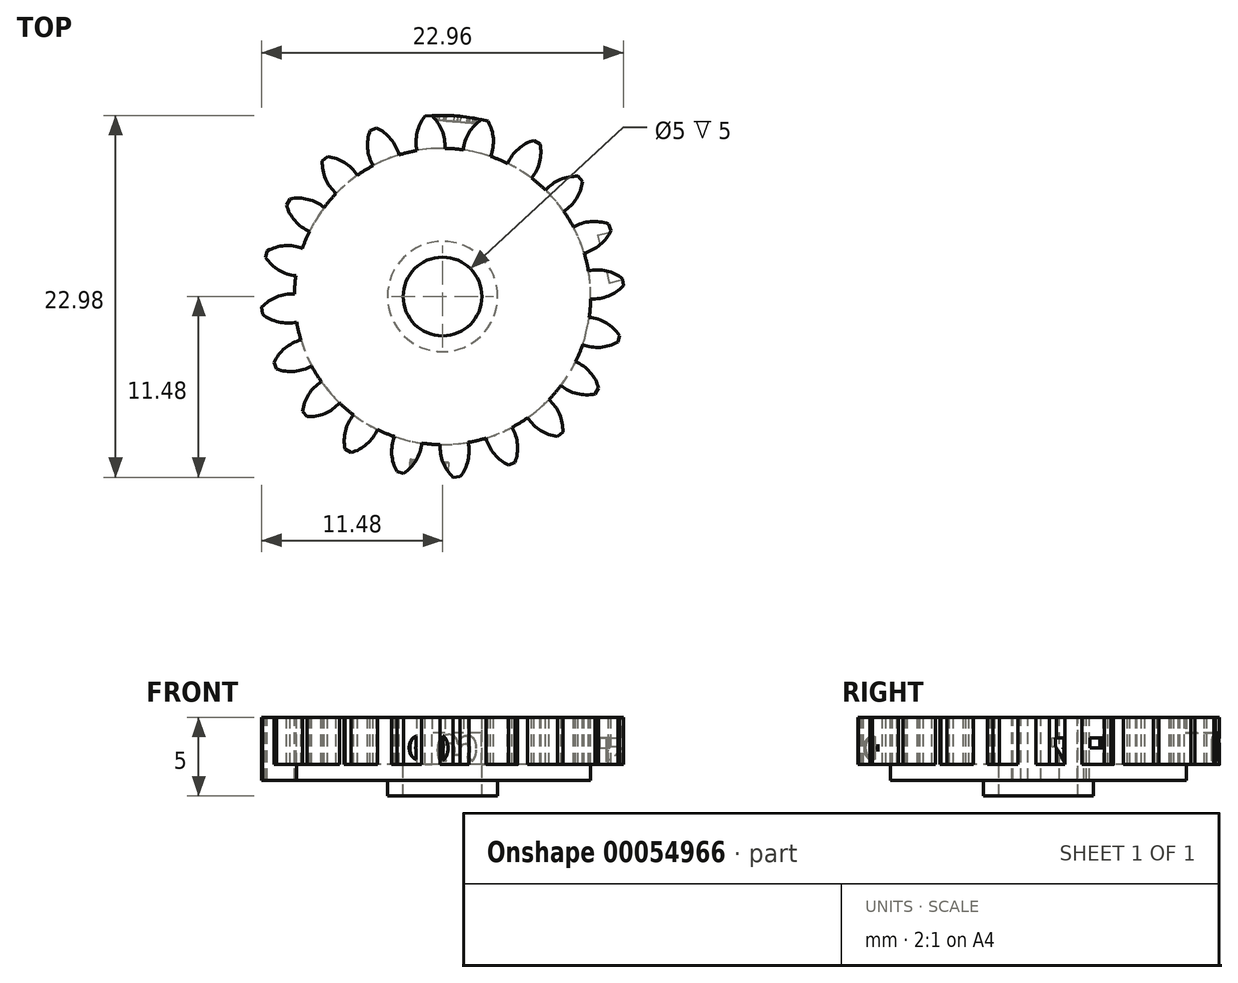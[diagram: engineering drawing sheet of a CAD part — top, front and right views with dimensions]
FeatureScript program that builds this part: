
annotation { "Feature Type Name" : "Feature", "Feature Type Description" : "" }
export const myFeature = defineFeature(function(context is Context, id is Id, definition is map)
    precondition{}
    {
        {
            assignVariable(context, id + "F0", {"name" : "GearDepth", "anyValue" : 1});
        }
        {
            var Q0;
            Q0=qCreatedBy(makeId("Top.planeOp"),FACE);
            var sketch = newSketch(context, id + "F1", { "sketchPlane" : qUnion([Q0])});
            skCircle(sketch, "E0", {"center": v(0, 0) * mm, "radius": 9.4 * mm});
            skCircle(sketch, "E1", {"center": v(0, 0) * mm, "radius": 10.45 * mm, "construction": true});
            skCircle(sketch, "E2", {"center": v(0, 0) * mm, "radius": 11.5 * mm});
            skLineSegment(sketch, "E3", {"start": v(0, 0) * mm, "end": v(0, 17.6) * mm, "construction": true});
            skLineSegment(sketch, "E4", {"start": v(0, 0) * mm, "end": v(-1.42, 18) * mm, "construction": true});
            skLineSegment(sketch, "E5", {"start": v(0, 10.45) * mm, "end": v(-10.54, 10.45) * mm, "construction": true});
            skLineSegment(sketch, "E6", {"start": v(0, 10.45) * mm, "end": v(-10.3, 6.7) * mm, "construction": true});
            skCircle(sketch, "E7", {"center": v(0, 10.45) * mm, "radius": 2.61 * mm, "construction": true});
            skCircle(sketch, "E8", {"center": v(-2.46, 9.56) * mm, "radius": 2.61 * mm, "construction": true});
            skArc(sketch, "E9", {"start": v(-4.91, 10.45) * mm, "mid": v(-4.92, 10.42) * mm, "end": v(-4.94, 10.39) * mm});
            skArc(sketch, "E10.trimOffspring", {"start": v(0.15, 9.4) * mm, "mid": v(-0.03, 10.54) * mm, "end": v(-0.68, 11.48) * mm});
            skArc(sketch, "E11.MirrorCS", {"start": v(-1.62, 9.27) * mm, "mid": v(-1.62, 10.41) * mm, "end": v(-1.12, 11.45) * mm});
            skLineSegment(sketch, "E12", {"start": v(-1.12, 11.45) * mm, "end": v(-0.68, 11.48) * mm});
            skArc(sketch, "E13.1.0", {"start": v(-2.76, 9) * mm, "mid": v(-3.29, 10.01) * mm, "end": v(-4.2, 10.7) * mm});
            skLineSegment(sketch, "E13.1.1", {"start": v(-4.6, 10.54) * mm, "end": v(-4.2, 10.7) * mm});
            skArc(sketch, "E13.1.2", {"start": v(-4.4, 8.31) * mm, "mid": v(-4.76, 9.4) * mm, "end": v(-4.6, 10.54) * mm});
            skArc(sketch, "E13.2.0", {"start": v(-5.4, 7.7) * mm, "mid": v(-6.22, 8.5) * mm, "end": v(-7.3, 8.89) * mm});
            skLineSegment(sketch, "E13.2.1", {"start": v(-7.64, 8.6) * mm, "end": v(-7.3, 8.89) * mm});
            skArc(sketch, "E13.2.2", {"start": v(-6.76, 6.54) * mm, "mid": v(-7.43, 7.47) * mm, "end": v(-7.64, 8.6) * mm});
            skArc(sketch, "E13.3.0", {"start": v(-7.52, 5.65) * mm, "mid": v(-8.54, 6.17) * mm, "end": v(-9.69, 6.2) * mm});
            skLineSegment(sketch, "E13.3.1", {"start": v(-9.92, 5.82) * mm, "end": v(-9.69, 6.2) * mm});
            skArc(sketch, "E13.3.2", {"start": v(-8.45, 4.13) * mm, "mid": v(-9.37, 4.81) * mm, "end": v(-9.92, 5.82) * mm});
            skArc(sketch, "E13.4.0", {"start": v(-8.9, 3.05) * mm, "mid": v(-10.03, 3.23) * mm, "end": v(-11.13, 2.9) * mm});
            skLineSegment(sketch, "E13.4.1", {"start": v(-11.23, 2.47) * mm, "end": v(-11.13, 2.9) * mm});
            skArc(sketch, "E13.4.2", {"start": v(-9.32, 1.32) * mm, "mid": v(-10.4, 1.68) * mm, "end": v(-11.23, 2.47) * mm});
            skArc(sketch, "E13.5.0", {"start": v(-9.4, 0.15) * mm, "mid": v(-10.54, -0.03) * mm, "end": v(-11.48, -0.68) * mm});
            skLineSegment(sketch, "E13.5.1", {"start": v(-11.45, -1.12) * mm, "end": v(-11.48, -0.68) * mm});
            skArc(sketch, "E13.5.2", {"start": v(-9.27, -1.62) * mm, "mid": v(-10.41, -1.62) * mm, "end": v(-11.45, -1.12) * mm});
            skArc(sketch, "E13.6.0", {"start": v(-9, -2.76) * mm, "mid": v(-10.01, -3.29) * mm, "end": v(-10.7, -4.2) * mm});
            skLineSegment(sketch, "E13.6.1", {"start": v(-10.54, -4.6) * mm, "end": v(-10.7, -4.2) * mm});
            skArc(sketch, "E13.6.2", {"start": v(-8.31, -4.4) * mm, "mid": v(-9.4, -4.76) * mm, "end": v(-10.54, -4.6) * mm});
            skArc(sketch, "E13.7.0", {"start": v(-7.7, -5.4) * mm, "mid": v(-8.5, -6.22) * mm, "end": v(-8.89, -7.3) * mm});
            skLineSegment(sketch, "E13.7.1", {"start": v(-8.6, -7.64) * mm, "end": v(-8.89, -7.3) * mm});
            skArc(sketch, "E13.7.2", {"start": v(-6.54, -6.76) * mm, "mid": v(-7.47, -7.43) * mm, "end": v(-8.6, -7.64) * mm});
            skArc(sketch, "E13.8.0", {"start": v(-5.65, -7.52) * mm, "mid": v(-6.17, -8.54) * mm, "end": v(-6.2, -9.69) * mm});
            skLineSegment(sketch, "E13.8.1", {"start": v(-5.82, -9.92) * mm, "end": v(-6.2, -9.69) * mm});
            skArc(sketch, "E13.8.2", {"start": v(-4.13, -8.45) * mm, "mid": v(-4.81, -9.37) * mm, "end": v(-5.82, -9.92) * mm});
            skArc(sketch, "E13.9.0", {"start": v(-3.05, -8.9) * mm, "mid": v(-3.23, -10.03) * mm, "end": v(-2.9, -11.13) * mm});
            skLineSegment(sketch, "E13.9.1", {"start": v(-2.47, -11.23) * mm, "end": v(-2.9, -11.13) * mm});
            skArc(sketch, "E13.9.2", {"start": v(-1.32, -9.32) * mm, "mid": v(-1.68, -10.4) * mm, "end": v(-2.47, -11.23) * mm});
            skArc(sketch, "E13.10.0", {"start": v(-0.15, -9.4) * mm, "mid": v(0.03, -10.54) * mm, "end": v(0.68, -11.48) * mm});
            skLineSegment(sketch, "E13.10.1", {"start": v(1.12, -11.45) * mm, "end": v(0.68, -11.48) * mm});
            skArc(sketch, "E13.10.2", {"start": v(1.62, -9.27) * mm, "mid": v(1.62, -10.41) * mm, "end": v(1.12, -11.45) * mm});
            skArc(sketch, "E13.11.0", {"start": v(2.76, -9) * mm, "mid": v(3.29, -10.01) * mm, "end": v(4.2, -10.7) * mm});
            skLineSegment(sketch, "E13.11.1", {"start": v(4.6, -10.54) * mm, "end": v(4.2, -10.7) * mm});
            skArc(sketch, "E13.11.2", {"start": v(4.4, -8.31) * mm, "mid": v(4.76, -9.4) * mm, "end": v(4.6, -10.54) * mm});
            skArc(sketch, "E13.12.0", {"start": v(5.4, -7.7) * mm, "mid": v(6.22, -8.5) * mm, "end": v(7.3, -8.89) * mm});
            skLineSegment(sketch, "E13.12.1", {"start": v(7.64, -8.6) * mm, "end": v(7.3, -8.89) * mm});
            skArc(sketch, "E13.12.2", {"start": v(6.76, -6.54) * mm, "mid": v(7.43, -7.47) * mm, "end": v(7.64, -8.6) * mm});
            skArc(sketch, "E13.13.0", {"start": v(7.52, -5.65) * mm, "mid": v(8.54, -6.17) * mm, "end": v(9.69, -6.2) * mm});
            skLineSegment(sketch, "E13.13.1", {"start": v(9.92, -5.82) * mm, "end": v(9.69, -6.2) * mm});
            skArc(sketch, "E13.13.2", {"start": v(8.45, -4.13) * mm, "mid": v(9.37, -4.81) * mm, "end": v(9.92, -5.82) * mm});
            skArc(sketch, "E13.14.0", {"start": v(8.9, -3.05) * mm, "mid": v(10.03, -3.23) * mm, "end": v(11.13, -2.9) * mm});
            skLineSegment(sketch, "E13.14.1", {"start": v(11.23, -2.47) * mm, "end": v(11.13, -2.9) * mm});
            skArc(sketch, "E13.14.2", {"start": v(9.32, -1.32) * mm, "mid": v(10.4, -1.68) * mm, "end": v(11.23, -2.47) * mm});
            skArc(sketch, "E13.15.0", {"start": v(9.4, -0.15) * mm, "mid": v(10.54, 0.03) * mm, "end": v(11.48, 0.68) * mm});
            skLineSegment(sketch, "E13.15.1", {"start": v(11.45, 1.12) * mm, "end": v(11.48, 0.68) * mm});
            skArc(sketch, "E13.15.2", {"start": v(9.27, 1.62) * mm, "mid": v(10.41, 1.62) * mm, "end": v(11.45, 1.12) * mm});
            skArc(sketch, "E13.16.0", {"start": v(9, 2.76) * mm, "mid": v(10.01, 3.29) * mm, "end": v(10.7, 4.2) * mm});
            skLineSegment(sketch, "E13.16.1", {"start": v(10.54, 4.6) * mm, "end": v(10.7, 4.2) * mm});
            skArc(sketch, "E13.16.2", {"start": v(8.31, 4.4) * mm, "mid": v(9.4, 4.76) * mm, "end": v(10.54, 4.6) * mm});
            skArc(sketch, "E13.17.0", {"start": v(7.7, 5.4) * mm, "mid": v(8.5, 6.22) * mm, "end": v(8.89, 7.3) * mm});
            skLineSegment(sketch, "E13.17.1", {"start": v(8.6, 7.64) * mm, "end": v(8.89, 7.3) * mm});
            skArc(sketch, "E13.17.2", {"start": v(6.54, 6.76) * mm, "mid": v(7.47, 7.43) * mm, "end": v(8.6, 7.64) * mm});
            skArc(sketch, "E13.18.0", {"start": v(5.65, 7.52) * mm, "mid": v(6.17, 8.54) * mm, "end": v(6.2, 9.69) * mm});
            skLineSegment(sketch, "E13.18.1", {"start": v(5.82, 9.92) * mm, "end": v(6.2, 9.69) * mm});
            skArc(sketch, "E13.18.2", {"start": v(4.13, 8.45) * mm, "mid": v(4.81, 9.37) * mm, "end": v(5.82, 9.92) * mm});
            skArc(sketch, "E13.19.0", {"start": v(3.05, 8.9) * mm, "mid": v(3.23, 10.03) * mm, "end": v(2.9, 11.13) * mm});
            skLineSegment(sketch, "E13.19.1", {"start": v(2.47, 11.23) * mm, "end": v(2.9, 11.13) * mm});
            skArc(sketch, "E13.19.2", {"start": v(1.32, 9.32) * mm, "mid": v(1.68, 10.4) * mm, "end": v(2.47, 11.23) * mm});
            skCircle(sketch, "E14", {"center": v(0, 0) * mm, "radius": 2.5 * mm});
            skCircle(sketch, "E15", {"center": v(0, 0) * mm, "radius": 3.5 * mm});
            skPoint(sketch, "E16", {"position": v(-11.47, 0.86) * mm});
            skSolve(sketch);
        }
        {
            var Q0;
            {var subQ0=sQuery(id+"F1.wireOp",EDGE,"E13.5.0");Q0=makeQuery(id+"F1.imprint","IMPRINT",FACE,{"disambiguationData":[TD([[makeQuery(id+"F1.imprint","IMPRINT",EDGE,{"derivedFrom":subQ0}),1.0]])]});}
            var Q1;
            {var subQ0=sQuery(id+"F1.wireOp",EDGE,"E13.4.0");Q1=makeQuery(id+"F1.imprint","IMPRINT",FACE,{"disambiguationData":[TD([[makeQuery(id+"F1.imprint","IMPRINT",EDGE,{"derivedFrom":subQ0}),1.0]])]});}
            var Q2;
            Q2=makeQuery(id+"F1.imprint","IMPRINT",FACE,{"disambiguationData":[TD([[makeQuery(id+"F1.imprint","IMPRINT",EDGE,{"derivedFrom":sQuery(id+"F1.wireOp",EDGE,"E14")}),-1.0]])]});
            var Q3;
            Q3=makeQuery(id+"F1.imprint","IMPRINT",FACE,{"disambiguationData":[TD([[makeQuery(id+"F1.imprint","IMPRINT",EDGE,{"derivedFrom":sQuery(id+"F1.wireOp",EDGE,"E15")}),-1.0]])]});
            extrude(context, id + "F2", {"entities" : qUnion([Q0, Q1, Q2, Q3]), "oppositeDirection" : true, "depth" : 3 * mm});
        }
        {
            var Q0;
            Q0=makeQuery(id+"F1.imprint","IMPRINT",FACE,{"disambiguationData":[TD([[makeQuery(id+"F1.imprint","IMPRINT",EDGE,{"derivedFrom":sQuery(id+"F1.wireOp",EDGE,"E14")}),-1.0]])]});
            var Q1;
            {var subQ0=sQuery(id+"F1.wireOp",EDGE,"E13.10.2");Q1=makeQuery(id+"F1.imprint","IMPRINT",FACE,{"disambiguationData":[TD([[makeQuery(id+"F1.imprint","IMPRINT",EDGE,{"derivedFrom":subQ0}),1.0]])]});}
            var Q2;
            {var subQ0=sQuery(id+"F1.wireOp",EDGE,"E13.11.0");Q2=makeQuery(id+"F1.imprint","IMPRINT",FACE,{"disambiguationData":[TD([[makeQuery(id+"F1.imprint","IMPRINT",EDGE,{"derivedFrom":subQ0}),1.0]])]});}
            var Q3;
            {var subQ0=sQuery(id+"F1.wireOp",EDGE,"E13.11.2");Q3=makeQuery(id+"F1.imprint","IMPRINT",FACE,{"disambiguationData":[TD([[makeQuery(id+"F1.imprint","IMPRINT",EDGE,{"derivedFrom":subQ0}),1.0]])]});}
            var Q4;
            {var subQ0=sQuery(id+"F1.wireOp",EDGE,"E13.12.0");Q4=makeQuery(id+"F1.imprint","IMPRINT",FACE,{"disambiguationData":[TD([[makeQuery(id+"F1.imprint","IMPRINT",EDGE,{"derivedFrom":subQ0}),1.0]])]});}
            var Q5;
            {var subQ0=sQuery(id+"F1.wireOp",EDGE,"E13.12.2");Q5=makeQuery(id+"F1.imprint","IMPRINT",FACE,{"disambiguationData":[TD([[makeQuery(id+"F1.imprint","IMPRINT",EDGE,{"derivedFrom":subQ0}),1.0]])]});}
            var Q6;
            {var subQ0=sQuery(id+"F1.wireOp",EDGE,"E13.13.0");Q6=makeQuery(id+"F1.imprint","IMPRINT",FACE,{"disambiguationData":[TD([[makeQuery(id+"F1.imprint","IMPRINT",EDGE,{"derivedFrom":subQ0}),1.0]])]});}
            var Q7;
            {var subQ0=sQuery(id+"F1.wireOp",EDGE,"E13.13.2");Q7=makeQuery(id+"F1.imprint","IMPRINT",FACE,{"disambiguationData":[TD([[makeQuery(id+"F1.imprint","IMPRINT",EDGE,{"derivedFrom":subQ0}),1.0]])]});}
            var Q8;
            {var subQ0=sQuery(id+"F1.wireOp",EDGE,"E13.14.0");Q8=makeQuery(id+"F1.imprint","IMPRINT",FACE,{"disambiguationData":[TD([[makeQuery(id+"F1.imprint","IMPRINT",EDGE,{"derivedFrom":subQ0}),1.0]])]});}
            var Q9;
            {var subQ0=sQuery(id+"F1.wireOp",EDGE,"E13.14.2");Q9=makeQuery(id+"F1.imprint","IMPRINT",FACE,{"disambiguationData":[TD([[makeQuery(id+"F1.imprint","IMPRINT",EDGE,{"derivedFrom":subQ0}),1.0]])]});}
            var Q10;
            {var subQ0=sQuery(id+"F1.wireOp",EDGE,"E13.15.0");Q10=makeQuery(id+"F1.imprint","IMPRINT",FACE,{"disambiguationData":[TD([[makeQuery(id+"F1.imprint","IMPRINT",EDGE,{"derivedFrom":subQ0}),1.0]])]});}
            var Q11;
            {var subQ0=sQuery(id+"F1.wireOp",EDGE,"E13.15.2");Q11=makeQuery(id+"F1.imprint","IMPRINT",FACE,{"disambiguationData":[TD([[makeQuery(id+"F1.imprint","IMPRINT",EDGE,{"derivedFrom":subQ0}),1.0]])]});}
            var Q12;
            {var subQ0=sQuery(id+"F1.wireOp",EDGE,"E13.16.0");Q12=makeQuery(id+"F1.imprint","IMPRINT",FACE,{"disambiguationData":[TD([[makeQuery(id+"F1.imprint","IMPRINT",EDGE,{"derivedFrom":subQ0}),1.0]])]});}
            var Q13;
            {var subQ0=sQuery(id+"F1.wireOp",EDGE,"E13.16.2");Q13=makeQuery(id+"F1.imprint","IMPRINT",FACE,{"disambiguationData":[TD([[makeQuery(id+"F1.imprint","IMPRINT",EDGE,{"derivedFrom":subQ0}),1.0]])]});}
            var Q14;
            {var subQ0=sQuery(id+"F1.wireOp",EDGE,"E13.17.0");Q14=makeQuery(id+"F1.imprint","IMPRINT",FACE,{"disambiguationData":[TD([[makeQuery(id+"F1.imprint","IMPRINT",EDGE,{"derivedFrom":subQ0}),1.0]])]});}
            var Q15;
            {var subQ0=sQuery(id+"F1.wireOp",EDGE,"E13.17.2");Q15=makeQuery(id+"F1.imprint","IMPRINT",FACE,{"disambiguationData":[TD([[makeQuery(id+"F1.imprint","IMPRINT",EDGE,{"derivedFrom":subQ0}),1.0]])]});}
            var Q16;
            {var subQ0=sQuery(id+"F1.wireOp",EDGE,"E13.18.0");Q16=makeQuery(id+"F1.imprint","IMPRINT",FACE,{"disambiguationData":[TD([[makeQuery(id+"F1.imprint","IMPRINT",EDGE,{"derivedFrom":subQ0}),1.0]])]});}
            var Q17;
            {var subQ0=sQuery(id+"F1.wireOp",EDGE,"E13.18.2");Q17=makeQuery(id+"F1.imprint","IMPRINT",FACE,{"disambiguationData":[TD([[makeQuery(id+"F1.imprint","IMPRINT",EDGE,{"derivedFrom":subQ0}),1.0]])]});}
            var Q18;
            {var subQ0=sQuery(id+"F1.wireOp",EDGE,"E13.19.0");Q18=makeQuery(id+"F1.imprint","IMPRINT",FACE,{"disambiguationData":[TD([[makeQuery(id+"F1.imprint","IMPRINT",EDGE,{"derivedFrom":subQ0}),1.0]])]});}
            var Q19;
            {var subQ0=sQuery(id+"F1.wireOp",EDGE,"E10.trimOffspring");Q19=makeQuery(id+"F1.imprint","IMPRINT",FACE,{"disambiguationData":[TD([[makeQuery(id+"F1.imprint","IMPRINT",EDGE,{"derivedFrom":subQ0}),-1.0]])]});}
            var Q20;
            {var subQ0=sQuery(id+"F1.wireOp",EDGE,"E10.trimOffspring");Q20=makeQuery(id+"F1.imprint","IMPRINT",FACE,{"disambiguationData":[TD([[makeQuery(id+"F1.imprint","IMPRINT",EDGE,{"derivedFrom":subQ0}),1.0]])]});}
            var Q21;
            {var subQ0=sQuery(id+"F1.wireOp",EDGE,"E11.MirrorCS");Q21=makeQuery(id+"F1.imprint","IMPRINT",FACE,{"disambiguationData":[TD([[makeQuery(id+"F1.imprint","IMPRINT",EDGE,{"derivedFrom":subQ0}),1.0]])]});}
            var Q22;
            {var subQ0=sQuery(id+"F1.wireOp",EDGE,"E13.1.0");Q22=makeQuery(id+"F1.imprint","IMPRINT",FACE,{"disambiguationData":[TD([[makeQuery(id+"F1.imprint","IMPRINT",EDGE,{"derivedFrom":subQ0}),1.0]])]});}
            var Q23;
            {var subQ0=sQuery(id+"F1.wireOp",EDGE,"E13.1.2");Q23=makeQuery(id+"F1.imprint","IMPRINT",FACE,{"disambiguationData":[TD([[makeQuery(id+"F1.imprint","IMPRINT",EDGE,{"derivedFrom":subQ0}),1.0]])]});}
            var Q24;
            {var subQ0=sQuery(id+"F1.wireOp",EDGE,"E13.2.0");Q24=makeQuery(id+"F1.imprint","IMPRINT",FACE,{"disambiguationData":[TD([[makeQuery(id+"F1.imprint","IMPRINT",EDGE,{"derivedFrom":subQ0}),1.0]])]});}
            var Q25;
            {var subQ0=sQuery(id+"F1.wireOp",EDGE,"E13.2.2");Q25=makeQuery(id+"F1.imprint","IMPRINT",FACE,{"disambiguationData":[TD([[makeQuery(id+"F1.imprint","IMPRINT",EDGE,{"derivedFrom":subQ0}),1.0]])]});}
            var Q26;
            {var subQ0=sQuery(id+"F1.wireOp",EDGE,"E13.3.0");Q26=makeQuery(id+"F1.imprint","IMPRINT",FACE,{"disambiguationData":[TD([[makeQuery(id+"F1.imprint","IMPRINT",EDGE,{"derivedFrom":subQ0}),1.0]])]});}
            var Q27;
            {var subQ0=sQuery(id+"F1.wireOp",EDGE,"E13.3.2");Q27=makeQuery(id+"F1.imprint","IMPRINT",FACE,{"disambiguationData":[TD([[makeQuery(id+"F1.imprint","IMPRINT",EDGE,{"derivedFrom":subQ0}),1.0]])]});}
            var Q28;
            {var subQ0=sQuery(id+"F1.wireOp",EDGE,"E13.4.0");Q28=makeQuery(id+"F1.imprint","IMPRINT",FACE,{"disambiguationData":[TD([[makeQuery(id+"F1.imprint","IMPRINT",EDGE,{"derivedFrom":subQ0}),1.0]])]});}
            var Q29;
            {var subQ0=sQuery(id+"F1.wireOp",EDGE,"E13.4.2");Q29=makeQuery(id+"F1.imprint","IMPRINT",FACE,{"disambiguationData":[TD([[makeQuery(id+"F1.imprint","IMPRINT",EDGE,{"derivedFrom":subQ0}),1.0]])]});}
            var Q30;
            {var subQ0=sQuery(id+"F1.wireOp",EDGE,"E13.5.0");Q30=makeQuery(id+"F1.imprint","IMPRINT",FACE,{"disambiguationData":[TD([[makeQuery(id+"F1.imprint","IMPRINT",EDGE,{"derivedFrom":subQ0}),1.0]])]});}
            var Q31;
            {var subQ0=sQuery(id+"F1.wireOp",EDGE,"E13.5.2");Q31=makeQuery(id+"F1.imprint","IMPRINT",FACE,{"disambiguationData":[TD([[makeQuery(id+"F1.imprint","IMPRINT",EDGE,{"derivedFrom":subQ0}),1.0]])]});}
            var Q32;
            {var subQ0=sQuery(id+"F1.wireOp",EDGE,"E13.6.0");Q32=makeQuery(id+"F1.imprint","IMPRINT",FACE,{"disambiguationData":[TD([[makeQuery(id+"F1.imprint","IMPRINT",EDGE,{"derivedFrom":subQ0}),1.0]])]});}
            var Q33;
            {var subQ0=sQuery(id+"F1.wireOp",EDGE,"E13.6.2");Q33=makeQuery(id+"F1.imprint","IMPRINT",FACE,{"disambiguationData":[TD([[makeQuery(id+"F1.imprint","IMPRINT",EDGE,{"derivedFrom":subQ0}),1.0]])]});}
            var Q34;
            {var subQ0=sQuery(id+"F1.wireOp",EDGE,"E13.7.0");Q34=makeQuery(id+"F1.imprint","IMPRINT",FACE,{"disambiguationData":[TD([[makeQuery(id+"F1.imprint","IMPRINT",EDGE,{"derivedFrom":subQ0}),1.0]])]});}
            var Q35;
            {var subQ0=sQuery(id+"F1.wireOp",EDGE,"E13.7.2");Q35=makeQuery(id+"F1.imprint","IMPRINT",FACE,{"disambiguationData":[TD([[makeQuery(id+"F1.imprint","IMPRINT",EDGE,{"derivedFrom":subQ0}),1.0]])]});}
            var Q36;
            {var subQ0=sQuery(id+"F1.wireOp",EDGE,"E13.8.0");Q36=makeQuery(id+"F1.imprint","IMPRINT",FACE,{"disambiguationData":[TD([[makeQuery(id+"F1.imprint","IMPRINT",EDGE,{"derivedFrom":subQ0}),1.0]])]});}
            var Q37;
            {var subQ0=sQuery(id+"F1.wireOp",EDGE,"E13.8.2");Q37=makeQuery(id+"F1.imprint","IMPRINT",FACE,{"disambiguationData":[TD([[makeQuery(id+"F1.imprint","IMPRINT",EDGE,{"derivedFrom":subQ0}),1.0]])]});}
            var Q38;
            {var subQ0=sQuery(id+"F1.wireOp",EDGE,"E13.9.0");Q38=makeQuery(id+"F1.imprint","IMPRINT",FACE,{"disambiguationData":[TD([[makeQuery(id+"F1.imprint","IMPRINT",EDGE,{"derivedFrom":subQ0}),1.0]])]});}
            var Q39;
            {var subQ0=sQuery(id+"F1.wireOp",EDGE,"E13.9.2");Q39=makeQuery(id+"F1.imprint","IMPRINT",FACE,{"disambiguationData":[TD([[makeQuery(id+"F1.imprint","IMPRINT",EDGE,{"derivedFrom":subQ0}),1.0]])]});}
            var Q40;
            {var subQ0=sQuery(id+"F1.wireOp",EDGE,"E13.10.0");Q40=makeQuery(id+"F1.imprint","IMPRINT",FACE,{"disambiguationData":[TD([[makeQuery(id+"F1.imprint","IMPRINT",EDGE,{"derivedFrom":subQ0}),1.0]])]});}
            var Q41;
            Q41=makeQuery(id+"F1.imprint","IMPRINT",FACE,{"disambiguationData":[TD([[makeQuery(id+"F1.imprint","IMPRINT",EDGE,{"derivedFrom":sQuery(id+"F1.wireOp",EDGE,"E15")}),-1.0]])]});
            extrude(context, id + "F3", {"entities" : qUnion([Q0, Q1, Q2, Q3, Q4, Q5, Q6, Q7, Q8, Q9, Q10, Q11, Q12, Q13, Q14, Q15, Q16, Q17, Q18, Q19, Q20, Q21, Q22, Q23, Q24, Q25, Q26, Q27, Q28, Q29, Q30, Q31, Q32, Q33, Q34, Q35, Q36, Q37, Q38, Q39, Q40, Q41]), "operationType" : NewBodyOperationType.ADD, "oppositeDirection" : true, "depth" : 2 * mm});
        }
        {
            var Q0;
            {var subQ0=sQuery(id+"F1.wireOp",EDGE,"E10.trimOffspring");Q0=makeQuery(id+"F1.imprint","IMPRINT",FACE,{"disambiguationData":[TD([[makeQuery(id+"F1.imprint","IMPRINT",EDGE,{"derivedFrom":subQ0}),1.0]])]});}
            var Q1;
            {var subQ0=sQuery(id+"F1.wireOp",EDGE,"E0");var subQ1=makeQuery(id+"F1.imprint","INTERSECT",VERTEX,{"derivedFrom":[subQ0,sQuery(id+"F1.wireOp",EDGE,"E10.trimOffspring")]});Q1=makeQuery(id+"F1.imprint","IMPRINT",FACE,{"disambiguationData":[TD([[makeQuery(id+"F1.imprint","IMPRINT",EDGE,{"disambiguationData":[TD([[subQ1,-1.0]])],"derivedFrom":subQ0}),1.0]])]});}
            var Q2;
            {var subQ0=sQuery(id+"F1.wireOp",EDGE,"E13.1.0");Q2=makeQuery(id+"F1.imprint","IMPRINT",FACE,{"disambiguationData":[TD([[makeQuery(id+"F1.imprint","IMPRINT",EDGE,{"derivedFrom":subQ0}),1.0]])]});}
            var Q3;
            {var subQ0=sQuery(id+"F1.wireOp",EDGE,"E13.2.0");Q3=makeQuery(id+"F1.imprint","IMPRINT",FACE,{"disambiguationData":[TD([[makeQuery(id+"F1.imprint","IMPRINT",EDGE,{"derivedFrom":subQ0}),1.0]])]});}
            var Q4;
            {var subQ0=sQuery(id+"F1.wireOp",EDGE,"E13.3.0");Q4=makeQuery(id+"F1.imprint","IMPRINT",FACE,{"disambiguationData":[TD([[makeQuery(id+"F1.imprint","IMPRINT",EDGE,{"derivedFrom":subQ0}),1.0]])]});}
            var Q5;
            {var subQ0=sQuery(id+"F1.wireOp",EDGE,"E13.4.0");Q5=makeQuery(id+"F1.imprint","IMPRINT",FACE,{"disambiguationData":[TD([[makeQuery(id+"F1.imprint","IMPRINT",EDGE,{"derivedFrom":subQ0}),1.0]])]});}
            var Q6;
            {var subQ0=sQuery(id+"F1.wireOp",EDGE,"E13.5.0");Q6=makeQuery(id+"F1.imprint","IMPRINT",FACE,{"disambiguationData":[TD([[makeQuery(id+"F1.imprint","IMPRINT",EDGE,{"derivedFrom":subQ0}),1.0]])]});}
            var Q7;
            {var subQ0=sQuery(id+"F1.wireOp",EDGE,"E13.6.0");Q7=makeQuery(id+"F1.imprint","IMPRINT",FACE,{"disambiguationData":[TD([[makeQuery(id+"F1.imprint","IMPRINT",EDGE,{"derivedFrom":subQ0}),1.0]])]});}
            var Q8;
            {var subQ0=sQuery(id+"F1.wireOp",EDGE,"E13.7.0");Q8=makeQuery(id+"F1.imprint","IMPRINT",FACE,{"disambiguationData":[TD([[makeQuery(id+"F1.imprint","IMPRINT",EDGE,{"derivedFrom":subQ0}),1.0]])]});}
            var Q9;
            {var subQ0=sQuery(id+"F1.wireOp",EDGE,"E13.8.0");Q9=makeQuery(id+"F1.imprint","IMPRINT",FACE,{"disambiguationData":[TD([[makeQuery(id+"F1.imprint","IMPRINT",EDGE,{"derivedFrom":subQ0}),1.0]])]});}
            var Q10;
            {var subQ0=sQuery(id+"F1.wireOp",EDGE,"E13.9.0");Q10=makeQuery(id+"F1.imprint","IMPRINT",FACE,{"disambiguationData":[TD([[makeQuery(id+"F1.imprint","IMPRINT",EDGE,{"derivedFrom":subQ0}),1.0]])]});}
            var Q11;
            {var subQ0=sQuery(id+"F1.wireOp",EDGE,"E13.10.0");Q11=makeQuery(id+"F1.imprint","IMPRINT",FACE,{"disambiguationData":[TD([[makeQuery(id+"F1.imprint","IMPRINT",EDGE,{"derivedFrom":subQ0}),1.0]])]});}
            var Q12;
            {var subQ0=sQuery(id+"F1.wireOp",EDGE,"E13.11.0");Q12=makeQuery(id+"F1.imprint","IMPRINT",FACE,{"disambiguationData":[TD([[makeQuery(id+"F1.imprint","IMPRINT",EDGE,{"derivedFrom":subQ0}),1.0]])]});}
            var Q13;
            {var subQ0=sQuery(id+"F1.wireOp",EDGE,"E13.12.0");Q13=makeQuery(id+"F1.imprint","IMPRINT",FACE,{"disambiguationData":[TD([[makeQuery(id+"F1.imprint","IMPRINT",EDGE,{"derivedFrom":subQ0}),1.0]])]});}
            var Q14;
            {var subQ0=sQuery(id+"F1.wireOp",EDGE,"E13.13.0");Q14=makeQuery(id+"F1.imprint","IMPRINT",FACE,{"disambiguationData":[TD([[makeQuery(id+"F1.imprint","IMPRINT",EDGE,{"derivedFrom":subQ0}),1.0]])]});}
            var Q15;
            {var subQ0=sQuery(id+"F1.wireOp",EDGE,"E13.14.0");Q15=makeQuery(id+"F1.imprint","IMPRINT",FACE,{"disambiguationData":[TD([[makeQuery(id+"F1.imprint","IMPRINT",EDGE,{"derivedFrom":subQ0}),1.0]])]});}
            var Q16;
            {var subQ0=sQuery(id+"F1.wireOp",EDGE,"E13.15.0");Q16=makeQuery(id+"F1.imprint","IMPRINT",FACE,{"disambiguationData":[TD([[makeQuery(id+"F1.imprint","IMPRINT",EDGE,{"derivedFrom":subQ0}),1.0]])]});}
            var Q17;
            {var subQ0=sQuery(id+"F1.wireOp",EDGE,"E13.16.0");Q17=makeQuery(id+"F1.imprint","IMPRINT",FACE,{"disambiguationData":[TD([[makeQuery(id+"F1.imprint","IMPRINT",EDGE,{"derivedFrom":subQ0}),1.0]])]});}
            var Q18;
            {var subQ0=sQuery(id+"F1.wireOp",EDGE,"E13.17.0");Q18=makeQuery(id+"F1.imprint","IMPRINT",FACE,{"disambiguationData":[TD([[makeQuery(id+"F1.imprint","IMPRINT",EDGE,{"derivedFrom":subQ0}),1.0]])]});}
            var Q19;
            {var subQ0=sQuery(id+"F1.wireOp",EDGE,"E13.18.0");Q19=makeQuery(id+"F1.imprint","IMPRINT",FACE,{"disambiguationData":[TD([[makeQuery(id+"F1.imprint","IMPRINT",EDGE,{"derivedFrom":subQ0}),1.0]])]});}
            var Q20;
            {var subQ0=sQuery(id+"F1.wireOp",EDGE,"E13.19.0");Q20=makeQuery(id+"F1.imprint","IMPRINT",FACE,{"disambiguationData":[TD([[makeQuery(id+"F1.imprint","IMPRINT",EDGE,{"derivedFrom":subQ0}),1.0]])]});}
            var Q21;
            Q21=makeQuery(id+"F1.imprint","IMPRINT",FACE,{"disambiguationData":[TD([[makeQuery(id+"F1.imprint","IMPRINT",EDGE,{"derivedFrom":sQuery(id+"F1.wireOp",EDGE,"E14")}),-1.0]])]});
            var Q22;
            Q22=sQuery(id+"F1.wireOp",EDGE,"E0");
            var Q23;
            Q23=sQuery(id+"F1.wireOp",EDGE,"E10.trimOffspring");
            var Q24;
            Q24=sQuery(id+"F1.wireOp",EDGE,"E12");
            var Q25;
            Q25=sQuery(id+"F1.wireOp",EDGE,"E11.MirrorCS");
            extrude(context, id + "F4", {"entities" : qUnion([Q0, Q1, Q2, Q3, Q4, Q5, Q6, Q7, Q8, Q9, Q10, Q11, Q12, Q13, Q14, Q15, Q16, Q17, Q18, Q19, Q20, Q21]), "operationType" : NewBodyOperationType.ADD, "surfaceEntities" : qUnion([Q22, Q23, Q24, Q25]), "depth" : (getVariable(context, 'GearDepth')) * mm});
        }
        {
            assignVariable(context, id + "F5", {"name" : "FontWidth", "anyValue" : 1.8});
        }
        {
            assignVariable(context, id + "F6", {"name" : "FontDepth", "anyValue" : .5});
        }
        {
            var Q0;
            Q0=makeQuery(id+"F3.opExtrude","SWEPT_EDGE",EDGE,{"disambiguationData":[OSD([sQuery(id+"F1.wireOp",EDGE,"E2"),sQuery(id+"F1.wireOp",EDGE,"E13.3.1"),sQuery(id+"F1.wireOp",EDGE,"E13.3.2")])]});
            var Q1;
            {var subQ0=sQuery(id+"F1.wireOp",EDGE,"E13.4.1");var subQ1=sQuery(id+"F1.wireOp",EDGE,"E13.4.0");var subQ2=sQuery(id+"F1.wireOp",EDGE,"E2");Q1=makeQuery(id+"F3.boolean.opBoolean","MERGE",EDGE,{"derivedFrom":[makeQuery(id+"F2.opExtrude","SWEPT_EDGE",EDGE,{"disambiguationData":[OSD([subQ2,subQ1,subQ0])]}),makeQuery(id+"F3.opExtrude","SWEPT_EDGE",EDGE,{"disambiguationData":[OSD([subQ2,subQ1,subQ0])]})]});}
            cPlane(context, id + "F7", {"entities" : qUnion([Q0, Q1]), "cplaneType" : CPlaneType.LINE_ANGLE, "offset" : 150 * mm, "angle" : 180 * degree, "width" : 150 * mm, "height" : 150 * mm});
        }
        {
            var Q0;
            Q0=qCreatedBy(id+"F7.planeOp",FACE);
            var sketch = newSketch(context, id + "F8", { "sketchPlane" : qUnion([Q0])});
            skText(sketch, "E17", { "text": "5", "fontName": "OpenSans-Bold.ttf"});
            skLineSegment(sketch, "E18", {"start": v(-0.48, -1.07) * mm, "end": v(0.42, -1.07) * mm, "construction": true});
            const initialGuessF8  = {"E17": [0.00118, -0.001, 0, 1, 0.0011]};
            skSetInitialGuess(sketch, initialGuessF8);
            skSolve(sketch);
        }
        {
            var Q0;
            Q0 = qSketchRegion(id + "F8", true);
            extrude(context, id + "F9", {"entities" : qUnion([Q0]), "operationType" : NewBodyOperationType.REMOVE, "endBound" : BoundingType.SYMMETRIC, "oppositeDirection" : true, "depth" : (getVariable(context, 'FontDepth')) * mm});
        }
        {
            var Q0;
            Q0=makeQuery(id+"F3.opExtrude","SWEPT_EDGE",EDGE,{"disambiguationData":[OSD([sQuery(id+"F1.wireOp",EDGE,"E2"),sQuery(id+"F1.wireOp",EDGE,"E13.1.1"),sQuery(id+"F1.wireOp",EDGE,"E13.1.2")])]});
            var Q1;
            Q1=makeQuery(id+"F3.opExtrude","SWEPT_EDGE",EDGE,{"disambiguationData":[OSD([sQuery(id+"F1.wireOp",EDGE,"E2"),sQuery(id+"F1.wireOp",EDGE,"E13.2.0"),sQuery(id+"F1.wireOp",EDGE,"E13.2.1")])]});
            cPlane(context, id + "F10", {"entities" : qUnion([Q0, Q1]), "cplaneType" : CPlaneType.LINE_ANGLE, "offset" : 150 * mm, "angle" : 180 * degree, "width" : 150 * mm, "height" : 150 * mm});
        }
        {
            var Q0;
            Q0=qCreatedBy(id+"F10.planeOp",FACE);
            var sketch = newSketch(context, id + "F11", { "sketchPlane" : qUnion([Q0])});
            skText(sketch, "E19", { "text": "4", "fontName": "OpenSans-Bold.ttf"});
            const initialGuessF11  = {"E19": [0.00118, -0.0016, 0, 1, 0.00233]};
            skSetInitialGuess(sketch, initialGuessF11);
            skSolve(sketch);
        }
        {
            var Q0;
            Q0 = qSketchRegion(id + "F11", true);
            extrude(context, id + "F12", {"entities" : qUnion([Q0]), "operationType" : NewBodyOperationType.REMOVE, "endBound" : BoundingType.SYMMETRIC, "oppositeDirection" : true, "depth" : (getVariable(context, 'FontDepth')) * mm});
        }
        {
            var Q0;
            Q0=makeQuery(id+"F3.opExtrude","SWEPT_EDGE",EDGE,{"disambiguationData":[OSD([sQuery(id+"F1.wireOp",EDGE,"E2"),sQuery(id+"F1.wireOp",EDGE,"E13.19.1"),sQuery(id+"F1.wireOp",EDGE,"E13.19.2")])]});
            var Q1;
            Q1=makeQuery(id+"F3.opExtrude","SWEPT_EDGE",EDGE,{"disambiguationData":[OSD([sQuery(id+"F1.wireOp",EDGE,"E2"),sQuery(id+"F1.wireOp",EDGE,"E10.trimOffspring"),sQuery(id+"F1.wireOp",EDGE,"E12")])]});
            cPlane(context, id + "F13", {"entities" : qUnion([Q0, Q1]), "cplaneType" : CPlaneType.LINE_ANGLE, "offset" : 150 * mm, "angle" : 180 * degree, "width" : 150 * mm, "height" : 150 * mm});
        }
        {
            var Q0;
            Q0=qCreatedBy(id+"F13.planeOp",FACE);
            var sketch = newSketch(context, id + "F14", { "sketchPlane" : qUnion([Q0])});
            skText(sketch, "E20", { "text": "3", "fontName": "OpenSans-Bold.ttf"});
            const initialGuessF14  = {"E20": [0.00118, -0.0019, 0, 1, 0.00244]};
            skSetInitialGuess(sketch, initialGuessF14);
            skSolve(sketch);
        }
        {
            var Q0;
            Q0 = qSketchRegion(id + "F14", true);
            extrude(context, id + "F15", {"entities" : qUnion([Q0]), "operationType" : NewBodyOperationType.REMOVE, "endBound" : BoundingType.SYMMETRIC, "oppositeDirection" : true, "depth" : (getVariable(context, 'FontDepth')) * mm});
        }
        {
            var Q0;
            Q0=makeQuery(id+"F3.opExtrude","SWEPT_EDGE",EDGE,{"disambiguationData":[OSD([sQuery(id+"F1.wireOp",EDGE,"E2"),sQuery(id+"F1.wireOp",EDGE,"E13.17.1"),sQuery(id+"F1.wireOp",EDGE,"E13.17.2")])]});
            var Q1;
            Q1=makeQuery(id+"F3.opExtrude","SWEPT_EDGE",EDGE,{"disambiguationData":[OSD([sQuery(id+"F1.wireOp",EDGE,"E2"),sQuery(id+"F1.wireOp",EDGE,"E13.18.0"),sQuery(id+"F1.wireOp",EDGE,"E13.18.1")])]});
            cPlane(context, id + "F16", {"entities" : qUnion([Q0, Q1]), "cplaneType" : CPlaneType.LINE_ANGLE, "offset" : 150 * mm, "angle" : 180 * degree, "width" : 150 * mm, "height" : 150 * mm});
        }
        {
            var Q0;
            Q0=qCreatedBy(id+"F16.planeOp",FACE);
            var sketch = newSketch(context, id + "F17", { "sketchPlane" : qUnion([Q0])});
            skText(sketch, "E21", { "text": "2", "fontName": "OpenSans-Bold.ttf"});
            const initialGuessF17  = {"E21": [0.00118, -0.0019, 0, 1, 0.0024]};
            skSetInitialGuess(sketch, initialGuessF17);
            skSolve(sketch);
        }
        {
            var Q0;
            Q0 = qSketchRegion(id + "F17", true);
            extrude(context, id + "F18", {"entities" : qUnion([Q0]), "operationType" : NewBodyOperationType.REMOVE, "endBound" : BoundingType.SYMMETRIC, "depth" : (getVariable(context, 'FontDepth')) * mm});
        }
        {
            var Q0;
            Q0=makeQuery(id+"F3.opExtrude","SWEPT_EDGE",EDGE,{"disambiguationData":[OSD([sQuery(id+"F1.wireOp",EDGE,"E2"),sQuery(id+"F1.wireOp",EDGE,"E13.15.1"),sQuery(id+"F1.wireOp",EDGE,"E13.15.2")])]});
            var Q1;
            Q1=makeQuery(id+"F3.opExtrude","SWEPT_EDGE",EDGE,{"disambiguationData":[OSD([sQuery(id+"F1.wireOp",EDGE,"E2"),sQuery(id+"F1.wireOp",EDGE,"E13.16.0"),sQuery(id+"F1.wireOp",EDGE,"E13.16.1")])]});
            cPlane(context, id + "F19", {"entities" : qUnion([Q0, Q1]), "cplaneType" : CPlaneType.LINE_ANGLE, "offset" : 150 * mm, "angle" : 180 * degree, "width" : 150 * mm, "height" : 150 * mm});
        }
        {
            var Q0;
            Q0=qCreatedBy(id+"F19.planeOp",FACE);
            var sketch = newSketch(context, id + "F20", { "sketchPlane" : qUnion([Q0])});
            skText(sketch, "E22", { "text": "1", "fontName": "OpenSans-Bold.ttf"});
            const initialGuessF20  = {"E22": [0.00148, -0.0021, 0, 1, 0.00314]};
            skSetInitialGuess(sketch, initialGuessF20);
            skSolve(sketch);
        }
        {
            var Q0;
            Q0 = qSketchRegion(id + "F20", true);
            extrude(context, id + "F21", {"entities" : qUnion([Q0]), "operationType" : NewBodyOperationType.REMOVE, "endBound" : BoundingType.SYMMETRIC, "oppositeDirection" : true, "depth" : (getVariable(context, 'FontWidth')) * mm});
        }
        {
            var Q0;
            Q0=makeQuery(id+"F3.opExtrude","SWEPT_EDGE",EDGE,{"disambiguationData":[OSD([sQuery(id+"F1.wireOp",EDGE,"E2"),sQuery(id+"F1.wireOp",EDGE,"E13.13.1"),sQuery(id+"F1.wireOp",EDGE,"E13.13.2")])]});
            var Q1;
            Q1=makeQuery(id+"F3.opExtrude","SWEPT_EDGE",EDGE,{"disambiguationData":[OSD([sQuery(id+"F1.wireOp",EDGE,"E2"),sQuery(id+"F1.wireOp",EDGE,"E13.14.0"),sQuery(id+"F1.wireOp",EDGE,"E13.14.1")])]});
            cPlane(context, id + "F22", {"entities" : qUnion([Q0, Q1]), "cplaneType" : CPlaneType.LINE_ANGLE, "offset" : 150 * mm, "angle" : 180 * degree, "width" : 150 * mm, "height" : 150 * mm});
        }
        {
            var Q0;
            Q0=qCreatedBy(id+"F22.planeOp",FACE);
            var sketch = newSketch(context, id + "F23", { "sketchPlane" : qUnion([Q0])});
            skText(sketch, "E23", { "text": "0", "fontName": "OpenSans-Bold.ttf"});
            const initialGuessF23  = {"E23": [0.00118, -0.0019, 0, 1, 0.00242]};
            skSetInitialGuess(sketch, initialGuessF23);
            skSolve(sketch);
        }
        {
            var Q0;
            Q0 = qSketchRegion(id + "F23", true);
            extrude(context, id + "F24", {"entities" : qUnion([Q0]), "operationType" : NewBodyOperationType.REMOVE, "endBound" : BoundingType.SYMMETRIC, "oppositeDirection" : true, "depth" : (getVariable(context, 'FontDepth')) * mm});
        }
        {
            var Q0;
            Q0=makeQuery(id+"F3.opExtrude","SWEPT_EDGE",EDGE,{"disambiguationData":[OSD([sQuery(id+"F1.wireOp",EDGE,"E2"),sQuery(id+"F1.wireOp",EDGE,"E13.11.1"),sQuery(id+"F1.wireOp",EDGE,"E13.11.2")])]});
            var Q1;
            Q1=makeQuery(id+"F3.opExtrude","SWEPT_EDGE",EDGE,{"disambiguationData":[OSD([sQuery(id+"F1.wireOp",EDGE,"E2"),sQuery(id+"F1.wireOp",EDGE,"E13.12.0"),sQuery(id+"F1.wireOp",EDGE,"E13.12.1")])]});
            cPlane(context, id + "F25", {"entities" : qUnion([Q0, Q1]), "cplaneType" : CPlaneType.LINE_ANGLE, "offset" : 150 * mm, "angle" : 180 * degree, "width" : 150 * mm, "height" : 150 * mm});
        }
        {
            var Q0;
            Q0=qCreatedBy(id+"F25.planeOp",FACE);
            var sketch = newSketch(context, id + "F26", { "sketchPlane" : qUnion([Q0])});
            skText(sketch, "E24", { "text": "9", "fontName": "OpenSans-Regular.ttf"});
            const initialGuessF26  = {"E24": [0.00118, -0.0019, 0, 1, 0.0025]};
            skSetInitialGuess(sketch, initialGuessF26);
            skSolve(sketch);
        }
        {
            var Q0;
            Q0 = qSketchRegion(id + "F26", true);
            extrude(context, id + "F27", {"entities" : qUnion([Q0]), "operationType" : NewBodyOperationType.REMOVE, "endBound" : BoundingType.SYMMETRIC, "oppositeDirection" : true, "depth" : (getVariable(context, 'FontDepth')) * mm});
        }
        {
            var Q0;
            Q0=makeQuery(id+"F3.opExtrude","SWEPT_EDGE",EDGE,{"disambiguationData":[OSD([sQuery(id+"F1.wireOp",EDGE,"E2"),sQuery(id+"F1.wireOp",EDGE,"E13.9.1"),sQuery(id+"F1.wireOp",EDGE,"E13.9.2")])]});
            var Q1;
            Q1=makeQuery(id+"F3.opExtrude","SWEPT_EDGE",EDGE,{"disambiguationData":[OSD([sQuery(id+"F1.wireOp",EDGE,"E2"),sQuery(id+"F1.wireOp",EDGE,"E13.10.0"),sQuery(id+"F1.wireOp",EDGE,"E13.10.1")])]});
            cPlane(context, id + "F28", {"entities" : qUnion([Q0, Q1]), "cplaneType" : CPlaneType.LINE_ANGLE, "offset" : 150 * mm, "angle" : 180 * degree, "width" : 150 * mm, "height" : 150 * mm});
        }
        {
            var Q0;
            Q0=qCreatedBy(id+"F28.planeOp",FACE);
            var sketch = newSketch(context, id + "F29", { "sketchPlane" : qUnion([Q0])});
            skText(sketch, "E25", { "text": "8\n", "fontName": "OpenSans-Bold.ttf"});
            const initialGuessF29  = {"E25": [0.00118, -0.0019, 0, 1, 0.00242]};
            skSetInitialGuess(sketch, initialGuessF29);
            skSolve(sketch);
        }
        {
            var Q0;
            Q0 = qSketchRegion(id + "F29", true);
            extrude(context, id + "F30", {"entities" : qUnion([Q0]), "operationType" : NewBodyOperationType.REMOVE, "endBound" : BoundingType.SYMMETRIC, "oppositeDirection" : true, "depth" : (getVariable(context, 'FontWidth')) * mm});
        }
        {
            var Q0;
            Q0=makeQuery(id+"F3.opExtrude","SWEPT_EDGE",EDGE,{"disambiguationData":[OSD([sQuery(id+"F1.wireOp",EDGE,"E2"),sQuery(id+"F1.wireOp",EDGE,"E13.7.1"),sQuery(id+"F1.wireOp",EDGE,"E13.7.2")])]});
            var Q1;
            Q1=makeQuery(id+"F3.opExtrude","SWEPT_EDGE",EDGE,{"disambiguationData":[OSD([sQuery(id+"F1.wireOp",EDGE,"E2"),sQuery(id+"F1.wireOp",EDGE,"E13.8.0"),sQuery(id+"F1.wireOp",EDGE,"E13.8.1")])]});
            cPlane(context, id + "F31", {"entities" : qUnion([Q0, Q1]), "cplaneType" : CPlaneType.LINE_ANGLE, "offset" : 150 * mm, "angle" : 180 * degree, "width" : 150 * mm, "height" : 150 * mm});
        }
        {
            var Q0;
            Q0=qCreatedBy(id+"F31.planeOp",FACE);
            var sketch = newSketch(context, id + "F32", { "sketchPlane" : qUnion([Q0])});
            skText(sketch, "E26", { "text": "7", "fontName": "OpenSans-Bold.ttf"});
            const initialGuessF32  = {"E26": [0.00118, -0.0019, 0, 1, 0.0024]};
            skSetInitialGuess(sketch, initialGuessF32);
            skSolve(sketch);
        }
        {
            var Q0;
            Q0 = qSketchRegion(id + "F32", true);
            extrude(context, id + "F33", {"entities" : qUnion([Q0]), "operationType" : NewBodyOperationType.REMOVE, "endBound" : BoundingType.SYMMETRIC, "oppositeDirection" : true, "depth" : (getVariable(context, 'FontDepth')) * mm});
        }
        {
            var Q0;
            {var subQ0=sQuery(id+"F1.wireOp",EDGE,"E13.5.2");var subQ1=sQuery(id+"F1.wireOp",EDGE,"E13.5.1");var subQ2=sQuery(id+"F1.wireOp",EDGE,"E2");Q0=makeQuery(id+"F3.boolean.opBoolean","MERGE",EDGE,{"derivedFrom":[makeQuery(id+"F2.opExtrude","SWEPT_EDGE",EDGE,{"disambiguationData":[OSD([subQ2,subQ1,subQ0])]}),makeQuery(id+"F3.opExtrude","SWEPT_EDGE",EDGE,{"disambiguationData":[OSD([subQ2,subQ1,subQ0])]})]});}
            var Q1;
            Q1=makeQuery(id+"F3.opExtrude","SWEPT_EDGE",EDGE,{"disambiguationData":[OSD([sQuery(id+"F1.wireOp",EDGE,"E2"),sQuery(id+"F1.wireOp",EDGE,"E13.6.0"),sQuery(id+"F1.wireOp",EDGE,"E13.6.1")])]});
            cPlane(context, id + "F34", {"entities" : qUnion([Q0, Q1]), "cplaneType" : CPlaneType.LINE_ANGLE, "offset" : 150 * mm, "angle" : 180 * degree, "width" : 150 * mm, "height" : 150 * mm});
        }
        {
            var Q0;
            Q0=qCreatedBy(id+"F34.planeOp",FACE);
            var sketch = newSketch(context, id + "F35", { "sketchPlane" : qUnion([Q0])});
            skText(sketch, "E27", { "text": "6", "fontName": "OpenSans-Bold.ttf"});
            const initialGuessF35  = {"E27": [0.00118, -0.0019, 0, 1, 0.0024]};
            skSetInitialGuess(sketch, initialGuessF35);
            skSolve(sketch);
        }
        {
            var Q0;
            Q0 = qSketchRegion(id + "F35", true);
            extrude(context, id + "F36", {"entities" : qUnion([Q0]), "operationType" : NewBodyOperationType.REMOVE, "endBound" : BoundingType.SYMMETRIC, "oppositeDirection" : true, "depth" : (getVariable(context, 'FontDepth')) * mm});
        }
        {
            var Q0;
            Q0=makeQuery(id+"F2.opExtrude","CAP_FACE",FACE,{"disambiguationData":[OSD([sQuery(id+"F1.wireOp",EDGE,"E0"),sQuery(id+"F1.wireOp",EDGE,"E13.4.0"),sQuery(id+"F1.wireOp",EDGE,"E13.4.1"),sQuery(id+"F1.wireOp",EDGE,"E13.4.2"),sQuery(id+"F1.wireOp",EDGE,"E13.5.0"),sQuery(id+"F1.wireOp",EDGE,"E13.5.1"),sQuery(id+"F1.wireOp",EDGE,"E13.5.2"),sQuery(id+"F1.wireOp",EDGE,"E14")])],"isStart":false});
            var sketch = newSketch(context, id + "F37", { "sketchPlane" : qUnion([Q0])});
            skCircle(sketch, "E28", {"center": v(0, 0) * mm, "radius": 3.5 * mm});
            skSolve(sketch);
        }
        {
            var Q0;
            Q0=makeQuery(id+"F37.imprint","IMPRINT",FACE,{"disambiguationData":[TD([[makeQuery(id+"F37.imprint","IMPRINT",EDGE,{"derivedFrom":sQuery(id+"F37.wireOp",EDGE,"E28")}),1.0]])]});
            extrude(context, id + "F38", {"entities" : qUnion([Q0]), "operationType" : NewBodyOperationType.ADD, "depth" : 1 * mm});
        }
    });
